# Revit family: PRD_FrankeWS_MnlCntrlSwtchs_KeySwitch_ZAQUA022
name_source: partatom
category: Electrical Fixtures
revit_build: Autodesk Revit 2018 (Build: 20190510_1515(x64)
units: mm (PartAtom-declared; Revit-internal decimal feet)

## family parameters
Cut with Voids When Loaded = No
Host = Face
Maintain Annotation Orientation = No
OmniClass Number = 23.80.50.11.14
OmniClass Title = Switches
Part Type = Normal
Room Calculation Point = No
Round Connector Dimension = Use Diameter
Shared = No

## types (1)
- ZAQUA022
    ApparentLoad = 0 VA
    AssetType = Fixed
    BIMObjectName = PRD_AR_ManualControlSwitches_KeySwitch_ZAQUA022
    BodyMaterial = PRD_AR_Black
    CasingMaterial = PRD_AR_SyntheticLightGrey
    Category = Pr_75_51_17_50, Manual control switches
    Default Elevation = 1500 mm  [stored 4.92126 ft]
    Description = Key switch, button for on-wall installation, lockable in both key positions, removable key. Maximum operating voltage 230 V AC.
    DurationUnit = year
    Features = lockable in both key positions, removable key
    GrossWeight = 0.28 kg
    HasLock = Yes
    IfcExportAs = IfcSwitchingDevice
    IfcExportType = USERDEFINED
    IsIlluminated = No
    Manufacturer = KWC Group AG
    ManufacturerName = KWC Group AG
    ManufacturerURL = www.kwc.com
www.kwc.com
    MaximumSwitchingVoltage = 230.00 V AC
    Model = ZAQUA022
    ModelNumber = 2000102675
    ModelReference = ZAQUA022
    NBSDescription = Manual control switches
    NBSReference = 90-65-50/450
    Name = Key switch ZAQUA022
    NetWeight = 0.16 kg
    NominalDepth = 56 mm  [stored 0.183727 ft]
    NominalHeight = 80 mm  [stored 0.262467 ft]
    NominalWidth = 72 mm  [stored 0.23622 ft]
    NumberOfGangs = 1
    OverallHeight = 225 mm  [stored 0.738189 ft]
    OverallLength = 12 mm  [stored 0.0393701 ft]
    OverallWidth = 205 mm  [stored 0.672572 ft]
    PowerFactor = 1
    ProductInformation = https://pim.kwc.com
    ProtectiveSystemIP = IP65
    Shape = Cuboid
    Size = 72 x 80 x 56 mm (W x H x D)
    Status = New
    TypeOfSwitch = Key switch
    URL = www.kwc.com
    Uniclass2015Code = Pr_75_51_17_50
    Uniclass2015Title = Manual control switches
    Uniclass2015Version = Products v1.17
    Version = 1
    Voltage = 230 V
    WarrantyDurationUnit = year

note: [stored X ft] marks values corroborated as IEEE doubles in the binary element streams (Revit-internal decimal feet)

## geometry (parser evidence)
native form markers: Sweep x5
no freeform markers — native parametric forms only
